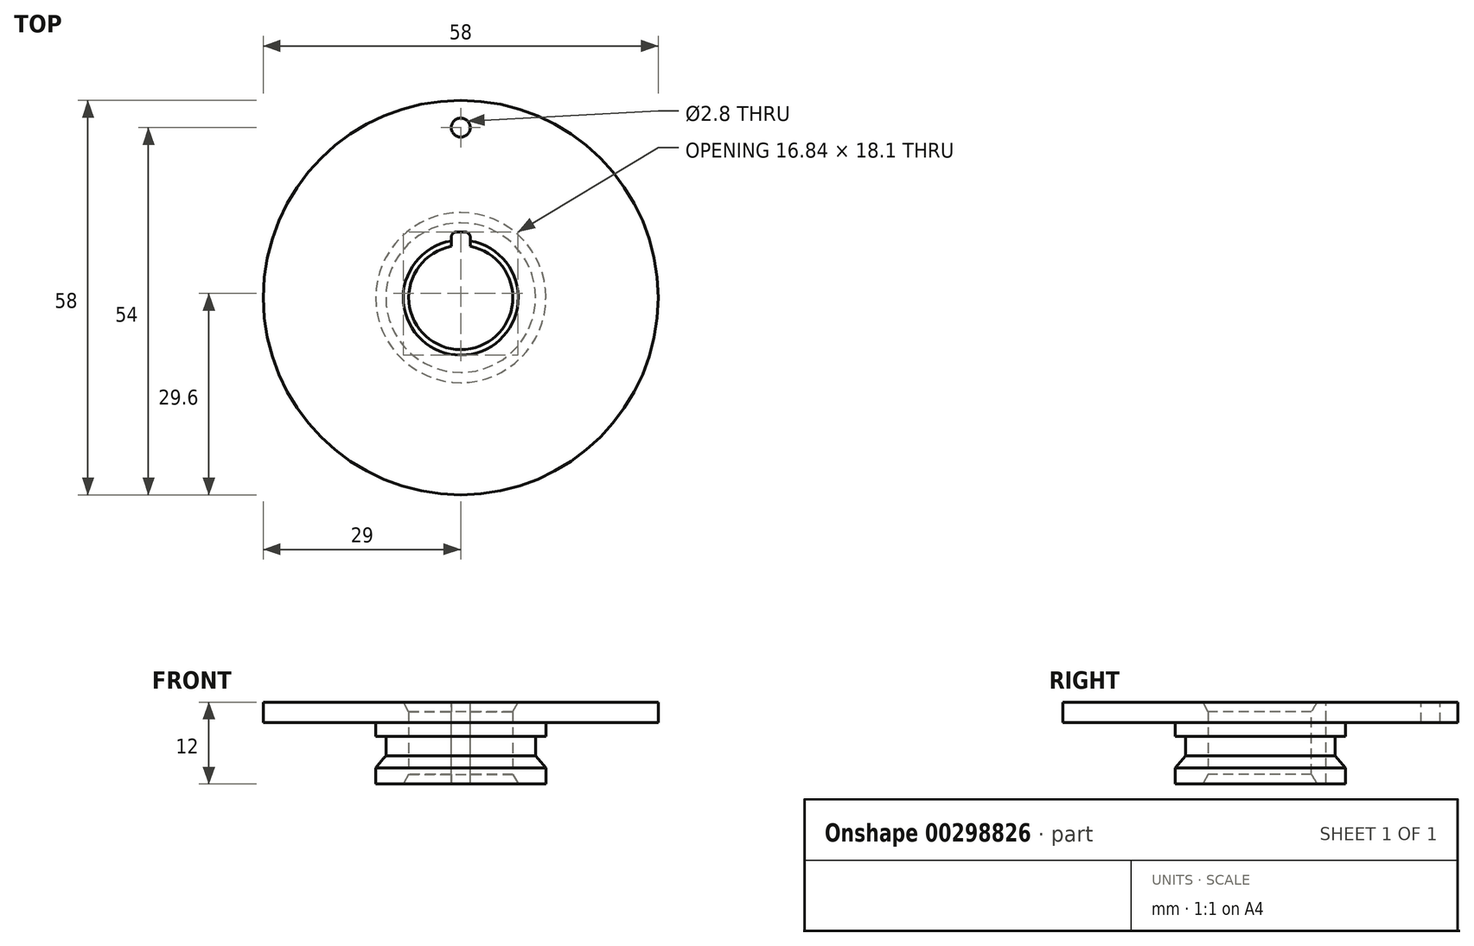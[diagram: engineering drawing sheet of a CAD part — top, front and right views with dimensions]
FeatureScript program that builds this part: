
annotation { "Feature Type Name" : "Feature", "Feature Type Description" : "" }
export const myFeature = defineFeature(function(context is Context, id is Id, definition is map)
    precondition{}
    {
        {
            var Q0;
            Q0=qCreatedBy(makeId("Right.planeOp"),FACE);
            var sketch = newSketch(context, id + "F0", { "sketchPlane" : qUnion([Q0])});
            skLineSegment(sketch, "E0", {"start": v(0, -304.05) * mm, "end": v(0, 160.16) * mm, "construction": true});
            skLineSegment(sketch, "E1", {"start": v(29, 0) * mm, "end": v(29, -3) * mm});
            skLineSegment(sketch, "E2", {"start": v(29, -3) * mm, "end": v(12.5, -3) * mm});
            skLineSegment(sketch, "E3", {"start": v(12.5, -3) * mm, "end": v(12.5, -5) * mm});
            skLineSegment(sketch, "E4", {"start": v(12.5, -5) * mm, "end": v(11, -5) * mm});
            skLineSegment(sketch, "E5", {"start": v(11, -5) * mm, "end": v(11, -10) * mm});
            skLineSegment(sketch, "E6", {"start": v(11, -10) * mm, "end": v(12.5, -10) * mm});
            skLineSegment(sketch, "E7", {"start": v(12.5, -10) * mm, "end": v(12.5, -12) * mm});
            skLineSegment(sketch, "E8", {"start": v(12.5, -12) * mm, "end": v(7.65, -12) * mm});
            skLineSegment(sketch, "E9", {"start": v(7.65, -12) * mm, "end": v(7.65, 0) * mm});
            skLineSegment(sketch, "E10", {"start": v(7.65, 0) * mm, "end": v(29, 0) * mm});
            skSolve(sketch);
        }
        {
            var Q0;
            Q0=makeQuery(id+"F0.imprint","IMPRINT",FACE,{"disambiguationData":[TD([[makeQuery(id+"F0.imprint","IMPRINT",EDGE,{"derivedFrom":sQuery(id+"F0.wireOp",EDGE,"E1")}),-1.0]])]});
            var Q1;
            Q1=sQuery(id+"F0.wireOp",EDGE,"E0");
            revolve(context, id + "F1", {"entities" : qUnion([Q0]), "axis" : qUnion([Q1]), "revolveType" : RevolveType.FULL});
        }
        {
            var Q0;
            Q0=makeQuery(id+"F1.opRevolve","SWEPT_FACE",FACE,{"disambiguationData":[OSD([sQuery(id+"F0.wireOp",EDGE,"E10")])]});
            var sketch = newSketch(context, id + "F2", { "sketchPlane" : qUnion([Q0])});
            skLineSegment(sketch, "E11.bottom", {"start": v(-1.4, 9.65) * mm, "end": v(1.4, 9.65) * mm});
            skLineSegment(sketch, "E11.top", {"start": v(-1.4, 7.52) * mm, "end": v(1.4, 7.52) * mm});
            skLineSegment(sketch, "E11.left", {"start": v(-1.4, 9.65) * mm, "end": v(-1.4, 7.52) * mm});
            skLineSegment(sketch, "E11.right", {"start": v(1.4, 9.65) * mm, "end": v(1.4, 7.52) * mm});
            skSolve(sketch);
        }
        {
            var Q0;
            Q0=makeQuery(id+"F2.imprint","IMPRINT",FACE,{"disambiguationData":[TD([[makeQuery(id+"F2.imprint","IMPRINT",EDGE,{"derivedFrom":sQuery(id+"F2.wireOp",EDGE,"E11.bottom")}),-1.0]])]});
            extrude(context, id + "F3", {"entities" : qUnion([Q0]), "operationType" : NewBodyOperationType.REMOVE, "oppositeDirection" : true, "depth" : 25 * mm});
        }
        {
            var Q0;
            Q0=makeQuery(id+"F3.boolean.opBoolean","COPY",EDGE,{"derivedFrom":makeQuery(id+"F3.opExtrude","SWEPT_EDGE",EDGE,{"disambiguationData":[OSD([sQuery(id+"F2.wireOp",EDGE,"E11.bottom"),sQuery(id+"F2.wireOp",EDGE,"E11.left")])]})});
            var Q1;
            Q1=makeQuery(id+"F3.boolean.opBoolean","COPY",EDGE,{"derivedFrom":makeQuery(id+"F3.opExtrude","SWEPT_EDGE",EDGE,{"disambiguationData":[OSD([sQuery(id+"F2.wireOp",EDGE,"E11.bottom"),sQuery(id+"F2.wireOp",EDGE,"E11.right")])]})});
            var Q2;
            Q2=makeQuery(id+"F3.boolean.opBoolean","COPY",EDGE,{"derivedFrom":makeQuery(id+"F3.opExtrude","SWEPT_EDGE",EDGE,{"disambiguationData":[OSD([sQuery(id+"F0.wireOp",EDGE,"E9"),sQuery(id+"F0.wireOp",EDGE,"E10"),sQuery(id+"F2.wireOp",EDGE,"E11.top"),sQuery(id+"F2.wireOp",EDGE,"E11.left")])]})});
            var Q3;
            Q3=makeQuery(id+"F3.boolean.opBoolean","COPY",EDGE,{"derivedFrom":makeQuery(id+"F3.opExtrude","SWEPT_EDGE",EDGE,{"disambiguationData":[OSD([sQuery(id+"F0.wireOp",EDGE,"E9"),sQuery(id+"F0.wireOp",EDGE,"E10"),sQuery(id+"F2.wireOp",EDGE,"E11.top"),sQuery(id+"F2.wireOp",EDGE,"E11.right")])]})});
            fillet(context, id + "F4", {"entities" : qUnion([Q0, Q1, Q2, Q3]), "radius" : 0.8 * mm, "tangentPropagation" : true, "allowEdgeOverflow" : false});
        }
        {
            var Q0;
            Q0=makeQuery(id+"F1.opRevolve","SWEPT_FACE",FACE,{"disambiguationData":[OSD([sQuery(id+"F0.wireOp",EDGE,"E10")])]});
            var sketch = newSketch(context, id + "F5", { "sketchPlane" : qUnion([Q0])});
            skCircle(sketch, "E12", {"center": v(0, 0) * mm, "radius": 25 * mm, "construction": true});
            skCircle(sketch, "E13", {"center": v(0, 25) * mm, "radius": 1.4 * mm});
            skSolve(sketch);
        }
        {
            var Q0;
            Q0=makeQuery(id+"F5.imprint","IMPRINT",FACE,{"disambiguationData":[TD([[makeQuery(id+"F5.imprint","IMPRINT",EDGE,{"derivedFrom":sQuery(id+"F5.wireOp",EDGE,"E13")}),1.0]])]});
            extrude(context, id + "F6", {"entities" : qUnion([Q0]), "operationType" : NewBodyOperationType.REMOVE, "oppositeDirection" : true, "depth" : 5 * mm});
        }
        {
            var Q0;
            {var subQ0=sQuery(id+"F0.wireOp",EDGE,"E9");var subQ1=sQuery(id+"F0.wireOp",EDGE,"E10");Q0=makeQuery(id+"Fk638RM6G5t4K3e_1.1.F3.boolean.opBoolean","SPLIT",EDGE,{"disambiguationData":[TD([makeQuery(id+"Fk638RM6G5t4K3e_1.1.F3.opExtrude","SWEPT_FACE",FACE,{"disambiguationData":[OSD([sQuery(id+"F2.wireOp",EDGE,"E11.right")])]})])],"derivedFrom":makeQuery(id+"F1.opRevolve","SWEPT_EDGE",EDGE,{"disambiguationData":[OSD([subQ0,subQ1])]})});}
            var Q1;
            {var subQ0=sQuery(id+"F0.wireOp",EDGE,"E8");var subQ1=sQuery(id+"F0.wireOp",EDGE,"E9");Q1=makeQuery(id+"Fk638RM6G5t4K3e_1.1.F3.boolean.opBoolean","SPLIT",EDGE,{"disambiguationData":[TD([makeQuery(id+"Fk638RM6G5t4K3e_1.1.F3.opExtrude","SWEPT_FACE",FACE,{"disambiguationData":[OSD([sQuery(id+"F2.wireOp",EDGE,"E11.right")])]})])],"derivedFrom":makeQuery(id+"F1.opRevolve","SWEPT_EDGE",EDGE,{"disambiguationData":[OSD([subQ0,subQ1])]})});}
            chamfer(context, id + "F7", {"entities" : qUnion([Q0, Q1]), "chamferType" : ChamferType.OFFSET_ANGLE, "width" : 0.8 * mm, "oppositeDirection" : false, "angle" : 60 * degree, "tangentPropagation" : true});
        }
        {
            var Q0;
            Q0=makeQuery(id+"F1.opRevolve","SWEPT_EDGE",EDGE,{"disambiguationData":[OSD([sQuery(id+"F0.wireOp",EDGE,"E5"),sQuery(id+"F0.wireOp",EDGE,"E6")])]});
            chamfer(context, id + "F8", {"entities" : qUnion([Q0]), "chamferType" : ChamferType.OFFSET_ANGLE, "width" : 1.8 * mm, "oppositeDirection" : false, "angle" : 50 * degree, "tangentPropagation" : true});
        }
    });
